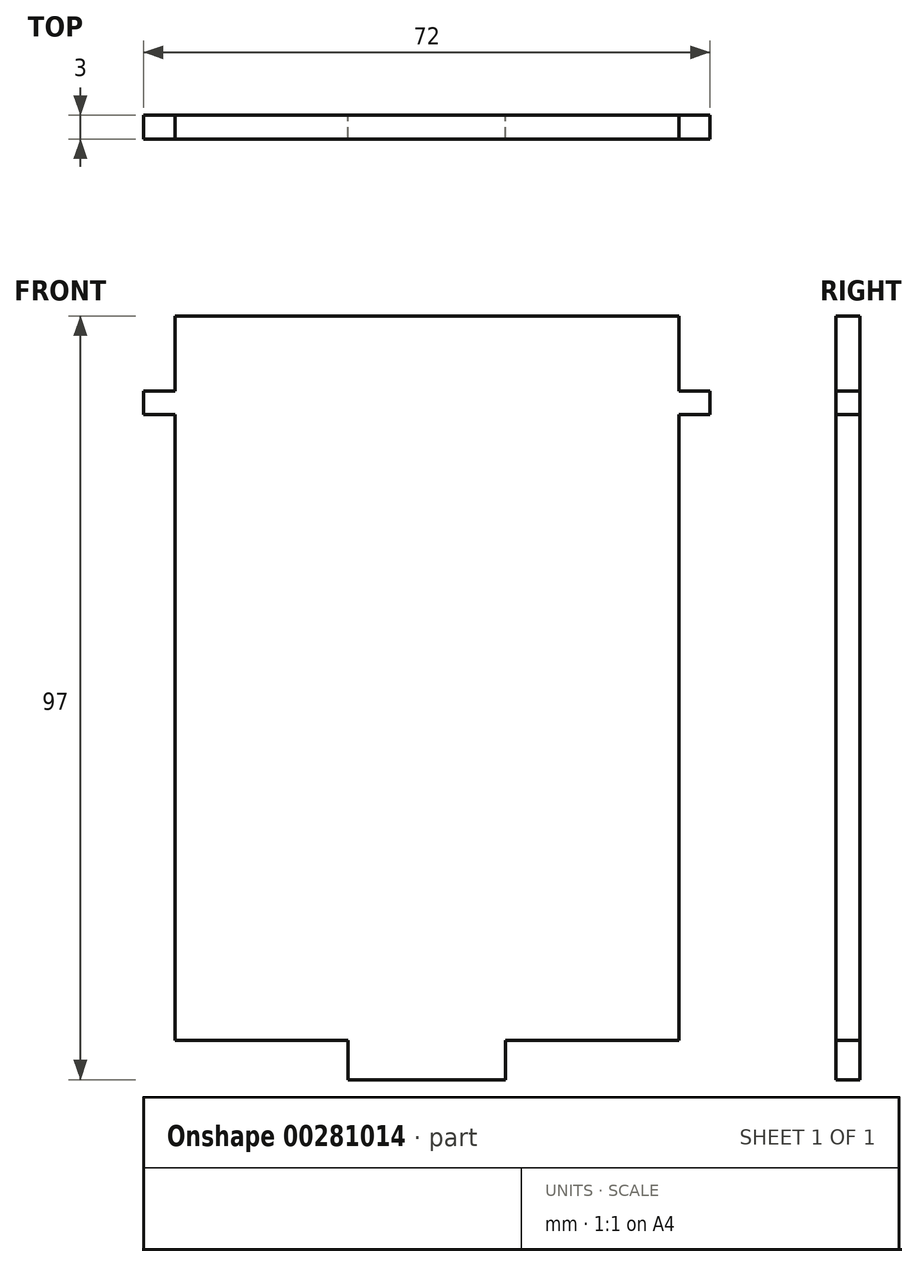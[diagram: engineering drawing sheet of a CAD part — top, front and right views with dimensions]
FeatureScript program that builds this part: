
annotation { "Feature Type Name" : "Feature", "Feature Type Description" : "" }
export const myFeature = defineFeature(function(context is Context, id is Id, definition is map)
    precondition{}
    {
        {
            var Q0;
            Q0=qCreatedBy(makeId("Front.planeOp"),FACE);
            var sketch = newSketch(context, id + "F0", { "sketchPlane" : qUnion([Q0])});
            skLineSegment(sketch, "E0.bottom", {"start": v(32, -46) * mm, "end": v(10, -46) * mm});
            skLineSegment(sketch, "E0.top", {"start": v(32, 46) * mm, "end": v(-32, 46) * mm});
            skLineSegment(sketch, "E0.left", {"start": v(32, -46) * mm, "end": v(32, 33.5) * mm});
            skLineSegment(sketch, "E0.right", {"start": v(-32, -46) * mm, "end": v(-32, 33.5) * mm});
            skPoint(sketch, "E0.middle", {"position": v(0, 0) * mm});
            skLineSegment(sketch, "E1.bottom", {"start": v(32, 36.5) * mm, "end": v(36, 36.5) * mm});
            skLineSegment(sketch, "E1.top", {"start": v(32, 33.5) * mm, "end": v(36, 33.5) * mm});
            skLineSegment(sketch, "E1.right", {"start": v(36, 36.5) * mm, "end": v(36, 33.5) * mm});
            skLineSegment(sketch, "E2.trimOffspring", {"start": v(32, 36.5) * mm, "end": v(32, 46) * mm});
            skLineSegment(sketch, "E3.MirrorCS", {"start": v(-32, 36.5) * mm, "end": v(-36, 36.5) * mm});
            skLineSegment(sketch, "E4.MirrorCS", {"start": v(-32, 33.5) * mm, "end": v(-36, 33.5) * mm});
            skLineSegment(sketch, "E5.MirrorCS", {"start": v(-36, 36.5) * mm, "end": v(-36, 33.5) * mm});
            skLineSegment(sketch, "E6.trimOffspring", {"start": v(-32, 36.5) * mm, "end": v(-32, 46) * mm});
            skLineSegment(sketch, "E7.top", {"start": v(10, -51) * mm, "end": v(-10, -51) * mm});
            skLineSegment(sketch, "E7.left", {"start": v(10, -46) * mm, "end": v(10, -51) * mm});
            skLineSegment(sketch, "E7.right", {"start": v(-10, -46) * mm, "end": v(-10, -51) * mm});
            skLineSegment(sketch, "E8.trimOffspring", {"start": v(-10, -46) * mm, "end": v(-32, -46) * mm});
            skSolve(sketch);
        }
        {
            var Q0;
            Q0 = qSketchRegion(id + "F0", true);
            extrude(context, id + "F1", {"entities" : qUnion([Q0]), "depth" : 3 * mm});
        }
    });
